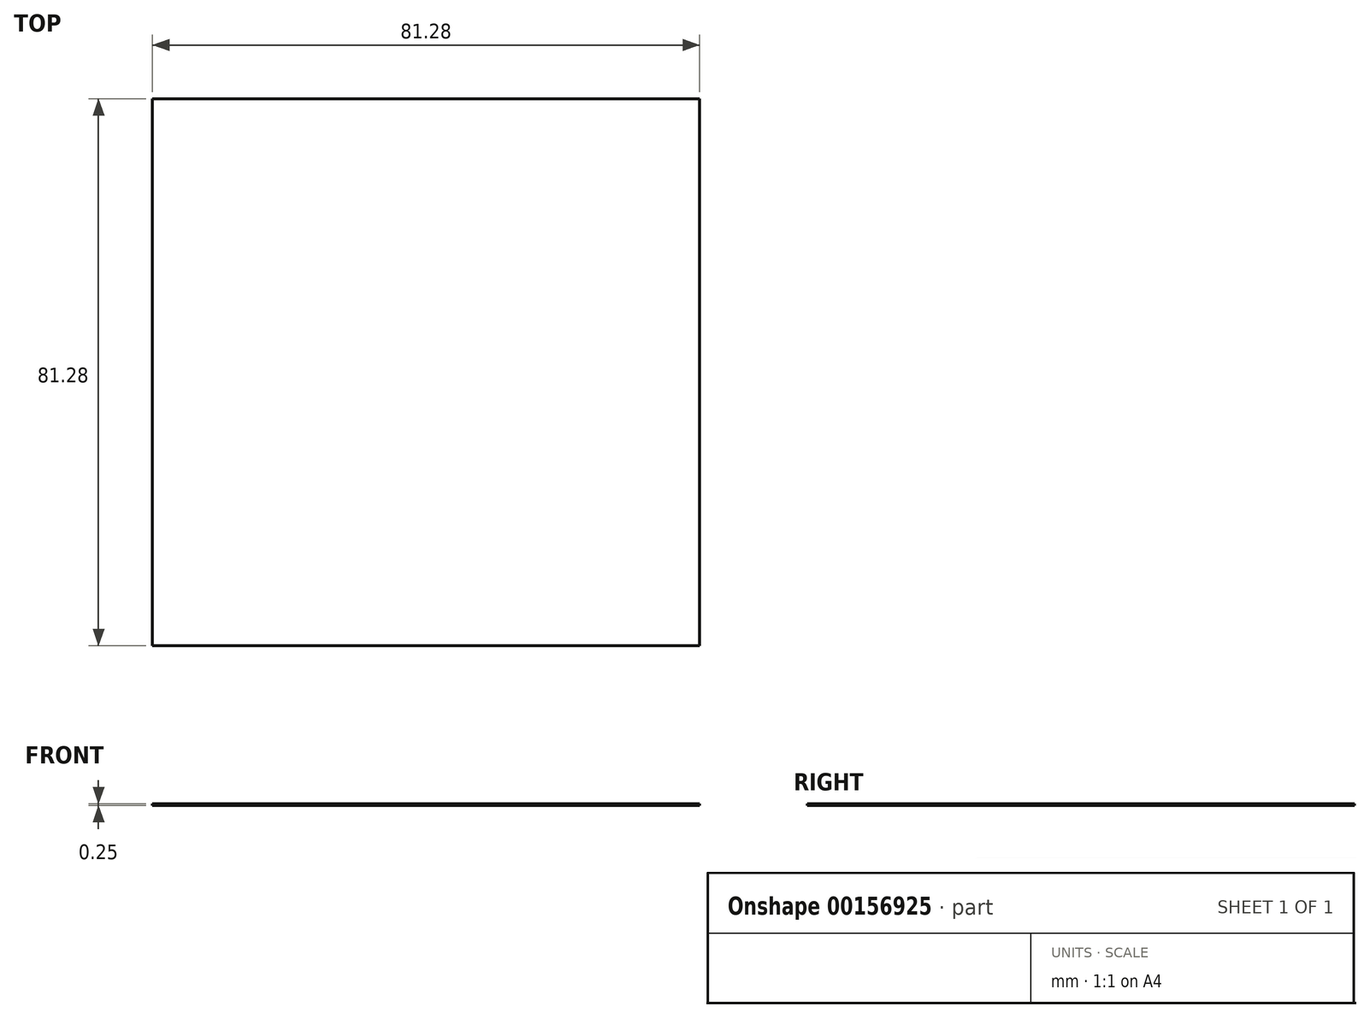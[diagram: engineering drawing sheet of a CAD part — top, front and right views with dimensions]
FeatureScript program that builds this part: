
annotation { "Feature Type Name" : "Feature", "Feature Type Description" : "" }
export const myFeature = defineFeature(function(context is Context, id is Id, definition is map)
    precondition{}
    {
        {
            var Q0;
            Q0=qCreatedBy(makeId("Top.planeOp"),FACE);
            var sketch = newSketch(context, id + "F0", { "sketchPlane" : qUnion([Q0])});
            skLineSegment(sketch, "E0.bottom", {"start": v(-40.64, 40.64) * mm, "end": v(40.64, 40.64) * mm});
            skLineSegment(sketch, "E0.top", {"start": v(-40.64, -40.64) * mm, "end": v(40.64, -40.64) * mm});
            skLineSegment(sketch, "E0.left", {"start": v(-40.64, 40.64) * mm, "end": v(-40.64, -40.64) * mm});
            skLineSegment(sketch, "E0.right", {"start": v(40.64, 40.64) * mm, "end": v(40.64, -40.64) * mm});
            skLineSegment(sketch, "E1", {"start": v(0, 40.64) * mm, "end": v(0, 0) * mm, "construction": true});
            skLineSegment(sketch, "E2", {"start": v(0, 0) * mm, "end": v(-40.64, 0) * mm, "construction": true});
            skSolve(sketch);
        }
        {
            var Q0;
            Q0=makeQuery(id+"F0.imprint","IMPRINT",FACE,{"disambiguationData":[TD([[makeQuery(id+"F0.imprint","IMPRINT",EDGE,{"derivedFrom":sQuery(id+"F0.wireOp",EDGE,"E0.bottom")}),-1.0]])]});
            extrude(context, id + "F1", {"entities" : qUnion([Q0]), "depth" : 0.25 * mm});
        }
    });
